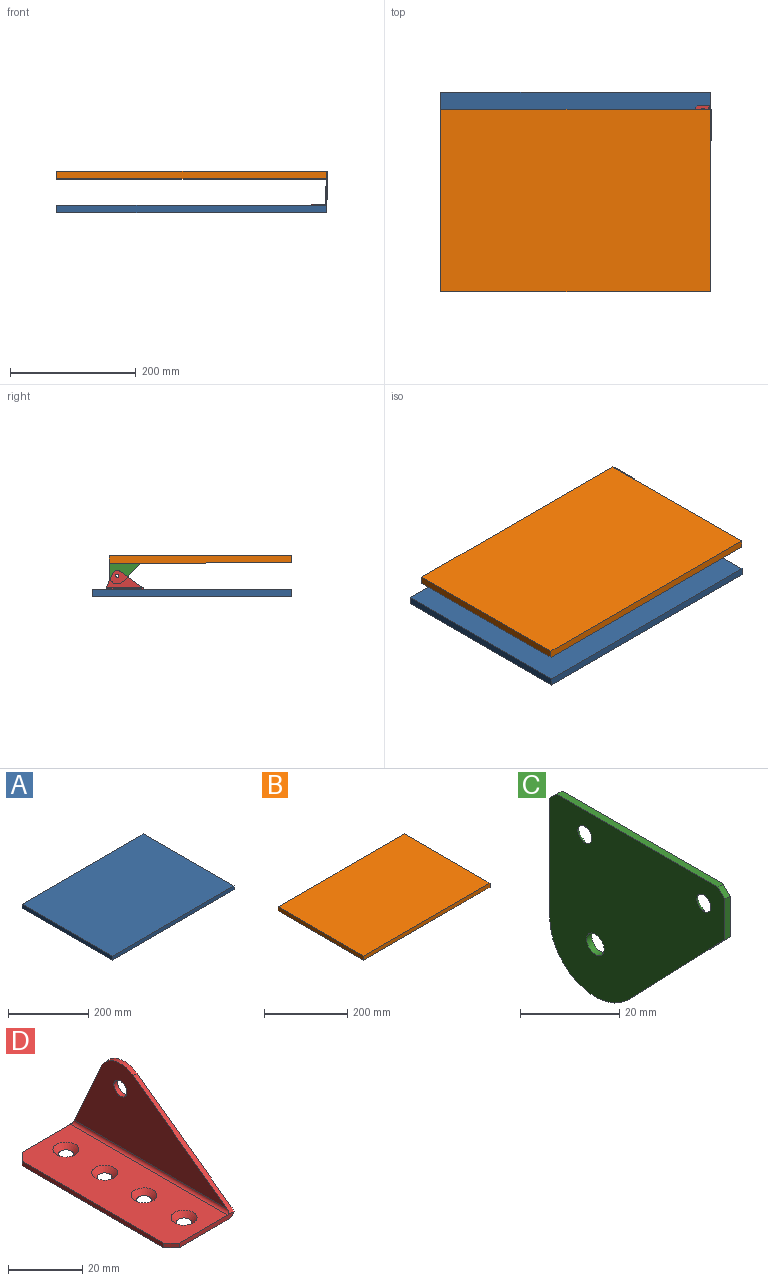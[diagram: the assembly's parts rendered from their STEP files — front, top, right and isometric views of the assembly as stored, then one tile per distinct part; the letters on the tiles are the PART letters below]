
ASSEMBLY  parts=4 mates=3
PART A: 6 faces, bbox 430x318x12 mm
  f0: plane 318x12mm, normal (1,0,0), area 3816mm2, adj f1,f3,f4,f5
  f1: plane 430x12mm, normal (0,1,0), area 5160mm2, adj f0,f2,f4,f5
  f2: plane 318x12mm, normal (-1,0,0), area 3816mm2, adj f1,f3,f4,f5
  f3: plane 430x12mm, normal (0,-1,0), area 5160mm2, adj f0,f2,f4,f5
  f4: plane 430x318mm, normal (0,0,1), area 136740mm2, adj f0,f1,f2,f3
  f5: plane 430x318mm, normal (0,0,-1), area 136740mm2, adj f0,f1,f2,f3
PART B: 6 faces, bbox 430x291x12 mm
  f0: plane 291x12mm, normal (1,0,0), area 3492mm2, adj f1,f3,f4,f5
  f1: plane 430x12mm, normal (0,1,0), area 5160mm2, adj f0,f2,f4,f5
  f2: plane 291x12mm, normal (-1,0,0), area 3492mm2, adj f1,f3,f4,f5
  f3: plane 430x12mm, normal (0,-1,0), area 5160mm2, adj f0,f2,f4,f5
  f4: plane 430x291mm, normal (0,0,1), area 125130mm2, adj f0,f1,f2,f3
  f5: plane 430x291mm, normal (0,0,-1), area 125130mm2, adj f0,f1,f2,f3
PART C: 12 faces, bbox 1.5x50x44.7 mm
  f0: plane 46x1.5mm, normal (0,0,1), area 69mm2, adj f6,f7,f10,f11
  f1: plane 10x1.5mm, normal (0,-1,0), area 15mm2, adj f2,f6,f7,f11
  f2: plane 28.67x27.64mm, normal (0,-0.72,-0.69), area 59.7mm2, adj f1,f3,f6,f7
  f3: cylinder r=13mm len=22.36mm, axis (-1,0,0), area 46.3mm2, adj f2,f4,f6,f7
  f4: plane 29.65x1.5mm, normal (0,1,0), area 44.5mm2, adj f3,f6,f7,f10
  f5: cylinder r=2.5mm len=5mm, axis (-1,0,0), area 23.6mm2, adj f6,f7
  f6: plane 50x44.65mm, normal (1,0,0), area 1577.9mm2, adj f0,f1,f2,f3,f4,f5,f8,f9
  f7: plane 50x44.65mm, normal (-1,0,0), area 1629.7mm2, adj f0,f1,f2,f3,f4,f5,f8,f9
  f8: cone r=2mm half-angle=45deg, axis (1,0,0), area 36.7mm2, adj f6,f7
  f9: cone r=2mm half-angle=45deg, axis (1,0,0), area 36.7mm2, adj f6,f7
  f10: plane 2x2mm, normal (0,0.71,0.71), area 4.2mm2, adj f0,f4,f6,f7
  f11: plane 2x2mm, normal (0,-0.71,0.71), area 4.2mm2, adj f0,f1,f6,f7
PART D: 19 faces, bbox 24x60x30 mm
  f0: plane 20.79x1.5mm, normal (0,-1,0), area 30.2mm2, adj f4,f6,f9,f12,f13
  f1: plane 58.18x27.5mm, normal (1,0,0), area 885.1mm2, adj f7,f8,f9,f10,f12
  f2: plane 58.18x27.5mm, normal (-1,0,0), area 885.1mm2, adj f7,f8,f9,f10,f11
  f3: plane 20.79x1.5mm, normal (0,1,0), area 30.2mm2, adj f4,f6,f7,f12,f14
  f4: plane 60x21.5mm, normal (0,0,-1), area 1230.7mm2, adj f0,f3,f5,f12,f13,f14,f15,f16
  f5: plane 54x1.5mm, normal (-1,0,0), area 81mm2, adj f4,f6,f13,f14
  f6: plane 60x21.5mm, normal (0,0,1), area 1127.1mm2, adj f0,f3,f5,f11,f13,f14,f15,f16
  f7: plane 23.6x10.47mm, normal (0,0.91,0.41), area 38.9mm2, adj f1,f2,f3,f8,f11,f12
  f8: cylinder r=8.25mm len=12.38mm, axis (1,0,0), area 22mm2, adj f1,f2,f7,f9
  f9: plane 37.16x26.93mm, normal (0,-0.59,0.81), area 69.1mm2, adj f0,f1,f2,f8,f11,f12
  f10: cylinder r=2.5mm len=5mm, axis (1,0,0), area 23.6mm2, adj f1,f2
  f11: cylinder r=1mm len=60mm, axis (0,-1,0), area 93.2mm2, adj f2,f6,f7,f9
  f12: cylinder r=2.5mm len=60mm, axis (0,1,0), area 234.7mm2, adj f0,f1,f3,f4,f7,f9
  f13: plane 3x3mm, normal (-0.71,-0.71,0), area 6.4mm2, adj f0,f4,f5,f6
  f14: plane 3x3mm, normal (-0.71,0.71,0), area 6.4mm2, adj f3,f4,f5,f6
  f15: cone r=2mm half-angle=45deg, axis (0,0,1), area 36.7mm2, adj f4,f6
  f16: cone r=2mm half-angle=45deg, axis (0,0,1), area 36.7mm2, adj f4,f6
  f17: cone r=2mm half-angle=45deg, axis (0,0,1), area 36.7mm2, adj f4,f6
  f18: cone r=2mm half-angle=45deg, axis (0,0,1), area 36.7mm2, adj f4,f6
PLACE A t=(20.41,-190.29,82.9)mm
PLACE B rot(axis=(-1,0,0),0.2deg) t=(20.16,-190.41,83.88)mm
PLACE C rot(axis=(-1,0,0),0.2deg) t=(20.16,-190.41,83.88)mm
PLACE D t=(20.16,-190.29,82.9)mm fixed
MATE revolute C.f3 <-> D.f8  axis (-1,0,0) through (20.16,87.71,116.65)mm
MATE fastened D.f18 <-> A.f4  axis (0,0,-1) through (8.41,98.21,94.9)mm
MATE fastened B.f0 <-> C.f8  axis (1,0,0) through (20.16,90.8,142.29)mm
